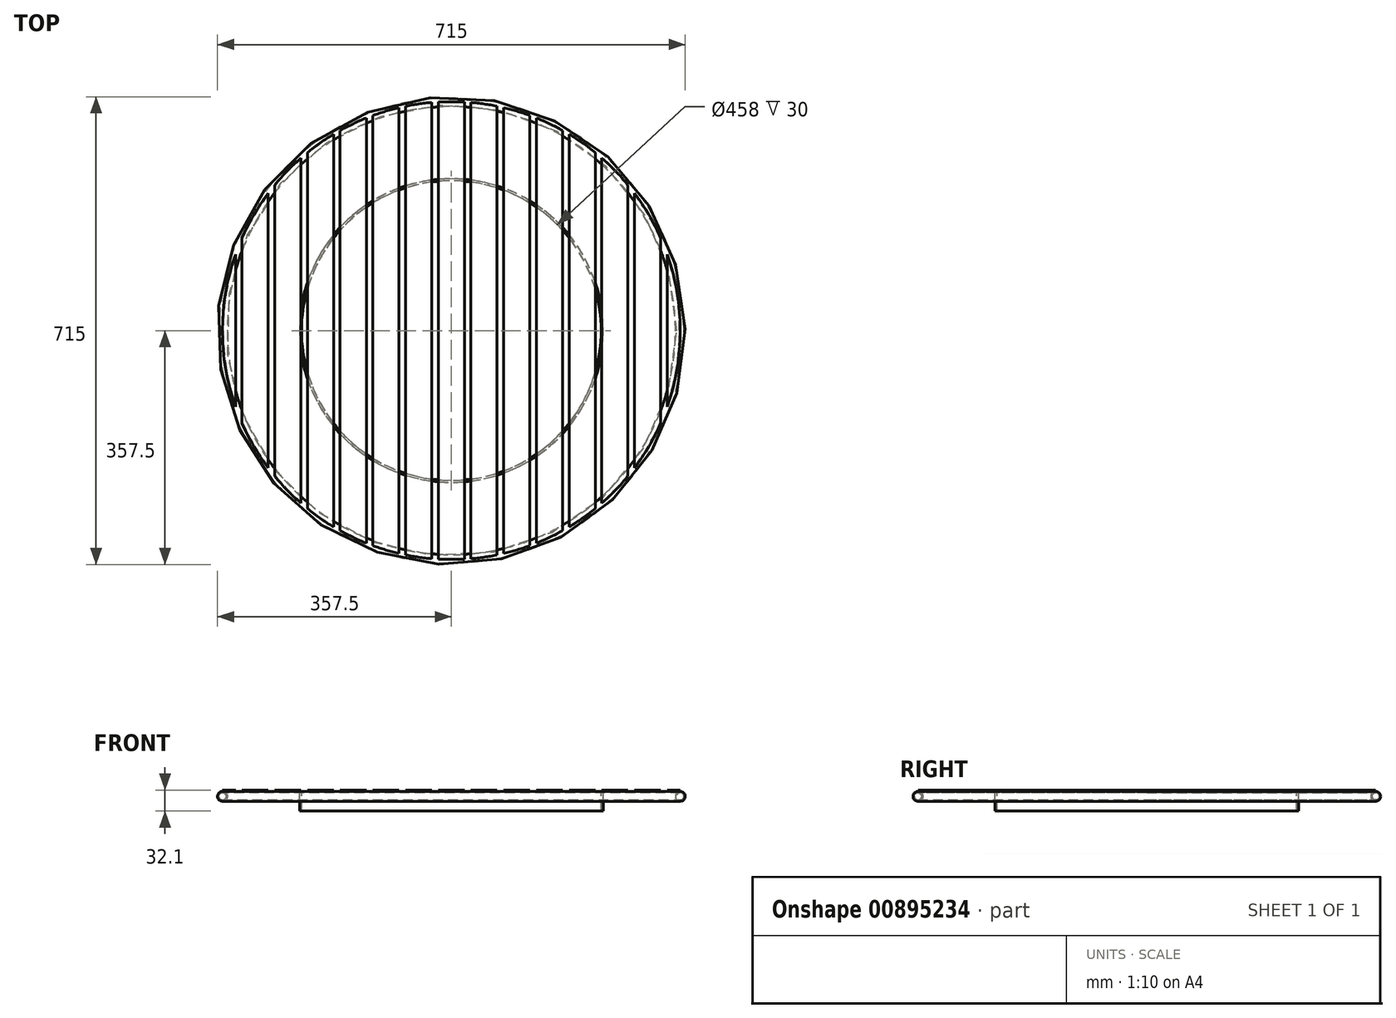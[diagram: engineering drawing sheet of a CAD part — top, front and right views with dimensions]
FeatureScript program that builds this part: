
annotation { "Feature Type Name" : "Feature", "Feature Type Description" : "" }
export const myFeature = defineFeature(function(context is Context, id is Id, definition is map)
    precondition{}
    {
        {
            var Q0;
            Q0=qCreatedBy(makeId("Top.planeOp"),FACE);
            var sketch = newSketch(context, id + "F0", { "sketchPlane" : qUnion([Q0])});
            skCircle(sketch, "E0", {"center": v(0, 0) * mm, "radius": 350 * mm});
            skSolve(sketch);
        }
        {
            var Q0;
            Q0=qCreatedBy(makeId("Front.planeOp"),FACE);
            var sketch = newSketch(context, id + "F1", { "sketchPlane" : qUnion([Q0])});
            skCircle(sketch, "E1", {"center": v(-350, 0) * mm, "radius": 7.5 * mm});
            skCircle(sketch, "E2", {"center": v(-350, 0) * mm, "radius": 5.5 * mm});
            skSolve(sketch);
        }
        {
            var Q0;
            Q0=makeQuery(id+"F1.imprint","IMPRINT",FACE,{"disambiguationData":[TD([[makeQuery(id+"F1.imprint","IMPRINT",EDGE,{"derivedFrom":sQuery(id+"F1.wireOp",EDGE,"E1")}),1.0]])]});
            var Q1;
            Q1=sQuery(id+"F0.wireOp",EDGE,"E0");
            sweep(context, id + "F2", {"profiles" : qUnion([Q0]), "path" : qUnion([Q1])});
        }
        {
            var Q0;
            Q0=qCreatedBy(makeId("Top.planeOp"),FACE);
            cPlane(context, id + "F3", {"entities" : qUnion([Q0]), "cplaneType" : CPlaneType.OFFSET, "offset" : 7.5 * mm, "width" : 150 * mm, "height" : 150 * mm});
        }
        {
            var Q0;
            Q0=qCreatedBy(id+"F3.planeOp",FACE);
            var sketch = newSketch(context, id + "F4", { "sketchPlane" : qUnion([Q0])});
            skCircle(sketch, "E3", {"center": v(0, 0) * mm, "radius": 350 * mm});
            skLineSegment(sketch, "E4.bottom", {"start": v(-20, 349.43) * mm, "end": v(20, 349.43) * mm});
            skLineSegment(sketch, "E4.top", {"start": v(-20, -349.43) * mm, "end": v(20, -349.43) * mm});
            skLineSegment(sketch, "E4.left", {"start": v(-20, 349.43) * mm, "end": v(-20, -349.43) * mm});
            skLineSegment(sketch, "E4.right", {"start": v(20, 349.43) * mm, "end": v(20, -349.43) * mm});
            skLineSegment(sketch, "E5.left", {"start": v(-30, 348.71) * mm, "end": v(-30, -348.71) * mm});
            skLineSegment(sketch, "E5.right", {"start": v(-70, 342.93) * mm, "end": v(-70, -342.93) * mm});
            skPoint(sketch, "E5.middle", {"position": v(-50, 0) * mm});
            skLineSegment(sketch, "E6.left", {"start": v(-80, 340.73) * mm, "end": v(-80, -340.73) * mm});
            skLineSegment(sketch, "E6.right", {"start": v(-120, 328.79) * mm, "end": v(-120, -328.79) * mm});
            skPoint(sketch, "E6.middle", {"position": v(-100, 0) * mm});
            skLineSegment(sketch, "E7.left", {"start": v(-130, 324.96) * mm, "end": v(-130, -324.96) * mm});
            skLineSegment(sketch, "E7.right", {"start": v(-170, 305.94) * mm, "end": v(-170, -305.94) * mm});
            skPoint(sketch, "E7.middle", {"position": v(-150, 0) * mm});
            skLineSegment(sketch, "E8.left", {"start": v(-180, 300.17) * mm, "end": v(-180, -300.17) * mm});
            skLineSegment(sketch, "E8.right", {"start": v(-220, 272.21) * mm, "end": v(-220, -272.21) * mm});
            skPoint(sketch, "E8.middle", {"position": v(-200, 0) * mm});
            skLineSegment(sketch, "E9.left", {"start": v(-230, 263.82) * mm, "end": v(-230, -263.82) * mm});
            skLineSegment(sketch, "E9.right", {"start": v(-270, 222.71) * mm, "end": v(-270, -222.71) * mm});
            skPoint(sketch, "E9.middle", {"position": v(-250, 0) * mm});
            skLineSegment(sketch, "E10", {"start": v(-280, -210) * mm, "end": v(-280, 210) * mm});
            skPoint(sketch, "E11.orphan", {"position": v(-270, 263.82) * mm});
            skPoint(sketch, "E12.orphan", {"position": v(-220, 300.17) * mm});
            skPoint(sketch, "E13.orphan", {"position": v(-170, 324.96) * mm});
            skPoint(sketch, "E14.orphan", {"position": v(-120, 340.73) * mm});
            skPoint(sketch, "E15.orphan", {"position": v(-70, 348.71) * mm});
            skPoint(sketch, "E5.top.end.orphan", {"position": v(-70, -348.71) * mm});
            skPoint(sketch, "E16.orphan", {"position": v(-120, -340.73) * mm});
            skPoint(sketch, "E17.orphan", {"position": v(-170, -324.96) * mm});
            skPoint(sketch, "E18.orphan", {"position": v(-220, -300.17) * mm});
            skPoint(sketch, "E9.top.end.orphan", {"position": v(-270, -263.82) * mm});
            skLineSegment(sketch, "E19", {"start": v(-320, 141.77) * mm, "end": v(-320, -141.77) * mm});
            skLineSegment(sketch, "E20", {"start": v(0, 0) * mm, "end": v(0, 56.7) * mm});
            skLineSegment(sketch, "E21.MirrorCS", {"start": v(30, 348.71) * mm, "end": v(30, -348.71) * mm});
            skLineSegment(sketch, "E22.MirrorCS", {"start": v(70, 342.93) * mm, "end": v(70, -342.93) * mm});
            skLineSegment(sketch, "E23.MirrorCS", {"start": v(80, 340.73) * mm, "end": v(80, -340.73) * mm});
            skLineSegment(sketch, "E24.MirrorCS", {"start": v(120, 328.79) * mm, "end": v(120, -328.79) * mm});
            skLineSegment(sketch, "E25.MirrorCS", {"start": v(130, 324.96) * mm, "end": v(130, -324.96) * mm});
            skLineSegment(sketch, "E26.MirrorCS", {"start": v(170, 305.94) * mm, "end": v(170, -305.94) * mm});
            skLineSegment(sketch, "E27.MirrorCS", {"start": v(180, 300.17) * mm, "end": v(180, -300.17) * mm});
            skLineSegment(sketch, "E28.MirrorCS", {"start": v(220, 272.21) * mm, "end": v(220, -272.21) * mm});
            skLineSegment(sketch, "E29.MirrorCS", {"start": v(230, 263.82) * mm, "end": v(230, -263.82) * mm});
            skLineSegment(sketch, "E30.MirrorCS", {"start": v(270, 222.71) * mm, "end": v(270, -222.71) * mm});
            skLineSegment(sketch, "E31.MirrorCS", {"start": v(320, 141.77) * mm, "end": v(320, -141.77) * mm});
            skLineSegment(sketch, "E32", {"start": v(-330, -116.62) * mm, "end": v(-330, 116.62) * mm});
            skLineSegment(sketch, "E33.MirrorCS", {"start": v(330, -116.62) * mm, "end": v(330, 116.62) * mm});
            skLineSegment(sketch, "E34.MirrorCS", {"start": v(280, -210) * mm, "end": v(280, 210) * mm});
            skSolve(sketch);
        }
        {
            var Q0;
            {var subQ0=sQuery(id+"F4.wireOp",EDGE,"E10");Q0=makeQuery(id+"F4.imprint","IMPRINT",FACE,{"disambiguationData":[TD([[makeQuery(id+"F4.imprint","IMPRINT",EDGE,{"derivedFrom":subQ0}),1.0]])]});}
            var Q1;
            {var subQ0=sQuery(id+"F4.wireOp",EDGE,"E9.left");Q1=makeQuery(id+"F4.imprint","IMPRINT",FACE,{"disambiguationData":[TD([[makeQuery(id+"F4.imprint","IMPRINT",EDGE,{"derivedFrom":subQ0}),-1.0]])]});}
            var Q2;
            {var subQ0=sQuery(id+"F4.wireOp",EDGE,"E8.left");Q2=makeQuery(id+"F4.imprint","IMPRINT",FACE,{"disambiguationData":[TD([[makeQuery(id+"F4.imprint","IMPRINT",EDGE,{"derivedFrom":subQ0}),-1.0]])]});}
            var Q3;
            {var subQ0=sQuery(id+"F4.wireOp",EDGE,"E7.left");Q3=makeQuery(id+"F4.imprint","IMPRINT",FACE,{"disambiguationData":[TD([[makeQuery(id+"F4.imprint","IMPRINT",EDGE,{"derivedFrom":subQ0}),-1.0]])]});}
            var Q4;
            {var subQ0=sQuery(id+"F4.wireOp",EDGE,"E6.left");Q4=makeQuery(id+"F4.imprint","IMPRINT",FACE,{"disambiguationData":[TD([[makeQuery(id+"F4.imprint","IMPRINT",EDGE,{"derivedFrom":subQ0}),-1.0]])]});}
            var Q5;
            {var subQ0=sQuery(id+"F4.wireOp",EDGE,"E5.left");Q5=makeQuery(id+"F4.imprint","IMPRINT",FACE,{"disambiguationData":[TD([[makeQuery(id+"F4.imprint","IMPRINT",EDGE,{"derivedFrom":subQ0}),-1.0]])]});}
            var Q6;
            Q6=makeQuery(id+"F4.imprint","IMPRINT",FACE,{"disambiguationData":[TD([[makeQuery(id+"F4.imprint","IMPRINT",EDGE,{"derivedFrom":sQuery(id+"F4.wireOp",EDGE,"E4.bottom")}),-1.0]])]});
            var Q7;
            {var subQ0=sQuery(id+"F4.wireOp",EDGE,"bfba225b-0817-4681-92a3-a46d2f063d4f0.MirrorCS");Q7=makeQuery(id+"F4.imprint","IMPRINT",FACE,{"disambiguationData":[TD([[makeQuery(id+"F4.imprint","IMPRINT",EDGE,{"derivedFrom":subQ0}),1.0]])]});}
            var Q8;
            {var subQ0=sQuery(id+"F4.wireOp",EDGE,"4912d06f-867c-44fb-9bcd-f5812b19cd6d0.MirrorCS");Q8=makeQuery(id+"F4.imprint","IMPRINT",FACE,{"disambiguationData":[TD([[makeQuery(id+"F4.imprint","IMPRINT",EDGE,{"derivedFrom":subQ0}),1.0]])]});}
            var Q9;
            {var subQ0=sQuery(id+"F4.wireOp",EDGE,"925a19c4-8f17-457f-9d0c-9387584e392c0.MirrorCS");Q9=makeQuery(id+"F4.imprint","IMPRINT",FACE,{"disambiguationData":[TD([[makeQuery(id+"F4.imprint","IMPRINT",EDGE,{"derivedFrom":subQ0}),1.0]])]});}
            var Q10;
            {var subQ0=sQuery(id+"F4.wireOp",EDGE,"22827606-f565-4dab-a49a-1f7b6423c8670.MirrorCS");Q10=makeQuery(id+"F4.imprint","IMPRINT",FACE,{"disambiguationData":[TD([[makeQuery(id+"F4.imprint","IMPRINT",EDGE,{"derivedFrom":subQ0}),1.0]])]});}
            var Q11;
            {var subQ0=sQuery(id+"F4.wireOp",EDGE,"55085a65-a3d1-4f32-8ddb-19d53a40a6160.MirrorCS");Q11=makeQuery(id+"F4.imprint","IMPRINT",FACE,{"disambiguationData":[TD([[makeQuery(id+"F4.imprint","IMPRINT",EDGE,{"derivedFrom":subQ0}),1.0]])]});}
            var Q12;
            {var subQ0=sQuery(id+"F4.wireOp",EDGE,"f9055472-6f82-4a08-91fa-8c525d6d7d5f0.MirrorCS");Q12=makeQuery(id+"F4.imprint","IMPRINT",FACE,{"disambiguationData":[TD([[makeQuery(id+"F4.imprint","IMPRINT",EDGE,{"derivedFrom":subQ0}),-1.0]])]});}
            var Q13;
            {var subQ0=sQuery(id+"F4.wireOp",EDGE,"E32");Q13=makeQuery(id+"F4.imprint","IMPRINT",FACE,{"disambiguationData":[TD([[makeQuery(id+"F4.imprint","IMPRINT",EDGE,{"derivedFrom":subQ0}),1.0]])]});}
            var Q14;
            {var subQ0=sQuery(id+"F4.wireOp",EDGE,"E21.MirrorCS");Q14=makeQuery(id+"F4.imprint","IMPRINT",FACE,{"disambiguationData":[TD([[makeQuery(id+"F4.imprint","IMPRINT",EDGE,{"derivedFrom":subQ0}),1.0]])]});}
            var Q15;
            {var subQ0=sQuery(id+"F4.wireOp",EDGE,"E23.MirrorCS");Q15=makeQuery(id+"F4.imprint","IMPRINT",FACE,{"disambiguationData":[TD([[makeQuery(id+"F4.imprint","IMPRINT",EDGE,{"derivedFrom":subQ0}),1.0]])]});}
            var Q16;
            {var subQ0=sQuery(id+"F4.wireOp",EDGE,"E25.MirrorCS");Q16=makeQuery(id+"F4.imprint","IMPRINT",FACE,{"disambiguationData":[TD([[makeQuery(id+"F4.imprint","IMPRINT",EDGE,{"derivedFrom":subQ0}),1.0]])]});}
            var Q17;
            {var subQ0=sQuery(id+"F4.wireOp",EDGE,"E27.MirrorCS");Q17=makeQuery(id+"F4.imprint","IMPRINT",FACE,{"disambiguationData":[TD([[makeQuery(id+"F4.imprint","IMPRINT",EDGE,{"derivedFrom":subQ0}),1.0]])]});}
            var Q18;
            {var subQ0=sQuery(id+"F4.wireOp",EDGE,"E29.MirrorCS");Q18=makeQuery(id+"F4.imprint","IMPRINT",FACE,{"disambiguationData":[TD([[makeQuery(id+"F4.imprint","IMPRINT",EDGE,{"derivedFrom":subQ0}),1.0]])]});}
            var Q19;
            {var subQ0=sQuery(id+"F4.wireOp",EDGE,"E33.MirrorCS");Q19=makeQuery(id+"F4.imprint","IMPRINT",FACE,{"disambiguationData":[TD([[makeQuery(id+"F4.imprint","IMPRINT",EDGE,{"derivedFrom":subQ0}),-1.0]])]});}
            var Q20;
            {var subQ0=sQuery(id+"F4.wireOp",EDGE,"E31.MirrorCS");Q20=makeQuery(id+"F4.imprint","IMPRINT",FACE,{"disambiguationData":[TD([[makeQuery(id+"F4.imprint","IMPRINT",EDGE,{"derivedFrom":subQ0}),-1.0]])]});}
            extrude(context, id + "F5", {"entities" : qUnion([Q0, Q1, Q2, Q3, Q4, Q5, Q6, Q7, Q8, Q9, Q10, Q11, Q12, Q13, Q14, Q15, Q16, Q17, Q18, Q19, Q20]), "operationType" : NewBodyOperationType.ADD, "depth" : 2 * mm, "offsetDistance" : 25 * mm, "hasSecondDirection" : true, "secondDirectionOppositeDirection" : true, "secondDirectionDepth" : .1 * mm});
        }
        {
            var Q0;
            Q0=makeQuery(id+"F5.opExtrude","CAP_FACE",FACE,{"disambiguationData":[OSD([sQuery(id+"F4.wireOp",EDGE,"E3"),sQuery(id+"F4.wireOp",EDGE,"E5.left"),sQuery(id+"F4.wireOp",EDGE,"E5.right")])],"isStart":true});
            var sketch = newSketch(context, id + "F6", { "sketchPlane" : qUnion([Q0])});
            skCircle(sketch, "E35", {"center": v(0, 0) * mm, "radius": 229 * mm});
            skCircle(sketch, "E36", {"center": v(0, 0) * mm, "radius": 232 * mm});
            skSolve(sketch);
        }
        {
            var Q0;
            Q0 = qSketchRegion(id + "F6", true);
            extrude(context, id + "F7", {"entities" : qUnion([Q0]), "operationType" : NewBodyOperationType.ADD, "depth" : 30 * mm, "offsetDistance" : 25 * mm});
        }
    });
